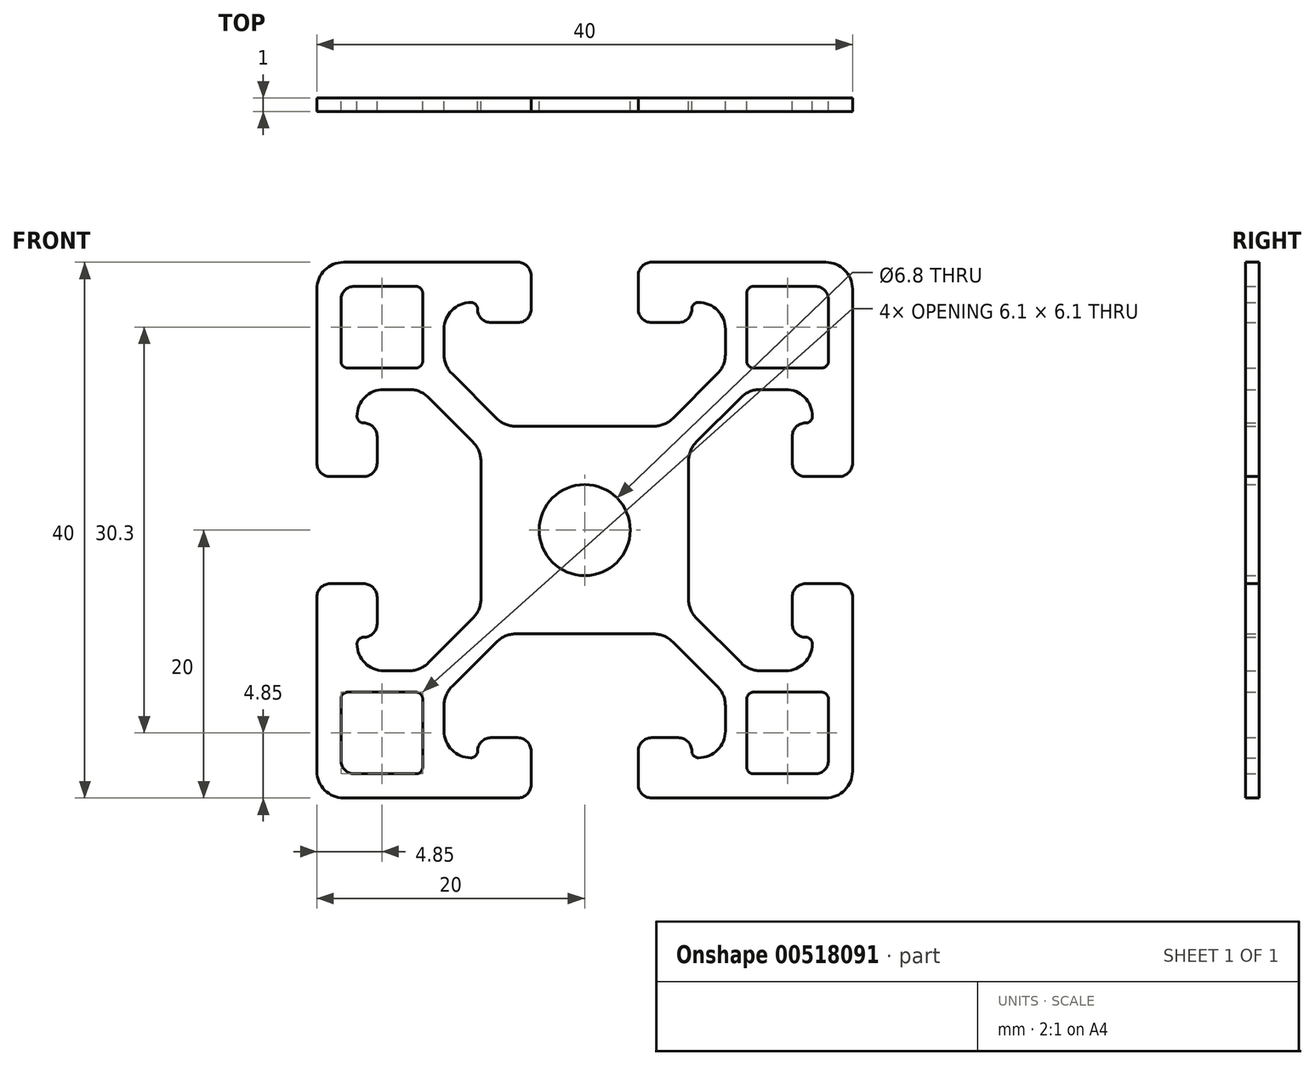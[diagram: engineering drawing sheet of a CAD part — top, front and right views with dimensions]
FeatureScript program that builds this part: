
annotation { "Feature Type Name" : "Feature", "Feature Type Description" : "" }
export const myFeature = defineFeature(function(context is Context, id is Id, definition is map)
    precondition{}
    {
        {
            var Q0;
            Q0=qCreatedBy(makeId("Front.planeOp"),FACE);
            var sketch = newSketch(context, id + "F0", { "sketchPlane" : qUnion([Q0])});
            skLineSegment(sketch, "E0", {"start": v(-20, 18) * mm, "end": v(-20, 5) * mm});
            skLineSegment(sketch, "E1", {"start": v(-19, 4) * mm, "end": v(-16.5, 4) * mm});
            skLineSegment(sketch, "E2", {"start": v(-15.5, 5) * mm, "end": v(-15.5, 7) * mm});
            skLineSegment(sketch, "E3", {"start": v(-16.5, 8) * mm, "end": v(-16.5, 8) * mm});
            skLineSegment(sketch, "E4", {"start": v(-2.4, 2.4) * mm, "end": v(-12.25, 12.25) * mm});
            skArc(sketch, "E5", {"start": v(-17, 8.5) * mm, "mid": v(-16.85, 8.15) * mm, "end": v(-16.5, 8) * mm});
            skArc(sketch, "E6", {"start": v(-15, 10.5) * mm, "mid": v(-16.41, 9.91) * mm, "end": v(-17, 8.5) * mm});
            skLineSegment(sketch, "E7", {"start": v(-15, 10.5) * mm, "end": v(-13.1, 10.5) * mm});
            skArc(sketch, "E8.filletArc", {"start": v(-20, 5) * mm, "mid": v(-19.7, 4.3) * mm, "end": v(-19, 4) * mm});
            skArc(sketch, "E9", {"start": v(-11.68, 9.91) * mm, "mid": v(-12.33, 10.35) * mm, "end": v(-13.1, 10.5) * mm});
            skLineSegment(sketch, "E10", {"start": v(-11.68, 9.91) * mm, "end": v(-8.34, 6.57) * mm});
            skArc(sketch, "E11", {"start": v(-8.34, 6.57) * mm, "mid": v(-7.9, 5.92) * mm, "end": v(-7.75, 5.15) * mm});
            skLineSegment(sketch, "E12", {"start": v(-18.2, 17.2) * mm, "end": v(-18.2, 12.6) * mm});
            skLineSegment(sketch, "E13", {"start": v(-17.7, 12.1) * mm, "end": v(-12.6, 12.1) * mm});
            skArc(sketch, "E14", {"start": v(-19.41, 19.41) * mm, "mid": v(-19.85, 18.77) * mm, "end": v(-20, 18) * mm});
            skArc(sketch, "E15", {"start": v(-17.9, 17.9) * mm, "mid": v(-18.12, 17.58) * mm, "end": v(-18.2, 17.2) * mm});
            skPoint(sketch, "E16.visualSharp", {"position": v(-15.5, 4) * mm});
            skArc(sketch, "E16.filletArc", {"start": v(-16.5, 4) * mm, "mid": v(-15.8, 4.3) * mm, "end": v(-15.5, 5) * mm});
            skPoint(sketch, "E17.visualSharp", {"position": v(-15.5, 8) * mm});
            skArc(sketch, "E17.filletArc", {"start": v(-15.5, 7) * mm, "mid": v(-15.8, 7.7) * mm, "end": v(-16.5, 8) * mm});
            skPoint(sketch, "E18.visualSharp", {"position": v(-18.2, 12.1) * mm});
            skArc(sketch, "E18.filletArc", {"start": v(-18.2, 12.6) * mm, "mid": v(-18.05, 12.25) * mm, "end": v(-17.7, 12.1) * mm});
            skArc(sketch, "E19", {"start": v(-12.6, 12.1) * mm, "mid": v(-12.4, 12.14) * mm, "end": v(-12.25, 12.25) * mm});
            skLineSegment(sketch, "E20.trimOffspring", {"start": v(-17.9, 17.9) * mm, "end": v(-19.41, 19.41) * mm});
            skLineSegment(sketch, "E21", {"start": v(-7.75, 5.15) * mm, "end": v(-7.75, 0) * mm});
            skLineSegment(sketch, "E22", {"start": v(-7.75, 0) * mm, "end": v(-3.4, 0) * mm});
            skArc(sketch, "E23", {"start": v(-2.4, 2.4) * mm, "mid": v(-3.14, 1.3) * mm, "end": v(-3.4, 0) * mm});
            skSolve(sketch);
        }
        {
            var Q0;
            Q0=makeQuery(id+"F0.imprint","IMPRINT",FACE,{"disambiguationData":[TD([[makeQuery(id+"F0.imprint","IMPRINT",EDGE,{"derivedFrom":sQuery(id+"F0.wireOp",EDGE,"E0")}),1.0]])]});
            extrude(context, id + "F1", {"entities" : qUnion([Q0]), "depth" : 1 * mm, "offsetDistance" : 25 * mm});
        }
        {
            var Q0;
            Q0=makeQuery(id+"F1.opExtrude","SWEPT_BODY",BODY,{"disambiguationData":[OSD([sQuery(id+"F0.wireOp",EDGE,"E0"),sQuery(id+"F0.wireOp",EDGE,"E1"),sQuery(id+"F0.wireOp",EDGE,"E2"),sQuery(id+"F0.wireOp",EDGE,"E3"),sQuery(id+"F0.wireOp",EDGE,"E4"),sQuery(id+"F0.wireOp",EDGE,"E5"),sQuery(id+"F0.wireOp",EDGE,"E6"),sQuery(id+"F0.wireOp",EDGE,"E7"),sQuery(id+"F0.wireOp",EDGE,"E8.filletArc"),sQuery(id+"F0.wireOp",EDGE,"E9"),sQuery(id+"F0.wireOp",EDGE,"E10"),sQuery(id+"F0.wireOp",EDGE,"E11"),sQuery(id+"F0.wireOp",EDGE,"E12"),sQuery(id+"F0.wireOp",EDGE,"E13"),sQuery(id+"F0.wireOp",EDGE,"E14"),sQuery(id+"F0.wireOp",EDGE,"E15"),sQuery(id+"F0.wireOp",EDGE,"E16.filletArc"),sQuery(id+"F0.wireOp",EDGE,"E17.filletArc"),sQuery(id+"F0.wireOp",EDGE,"E18.filletArc"),sQuery(id+"F0.wireOp",EDGE,"E19"),sQuery(id+"F0.wireOp",EDGE,"E20.trimOffspring"),sQuery(id+"F0.wireOp",EDGE,"E21"),sQuery(id+"F0.wireOp",EDGE,"E22"),sQuery(id+"F0.wireOp",EDGE,"E23")])]});
            var Q1;
            Q1=makeQuery(id+"F1.opExtrude","SWEPT_FACE",FACE,{"disambiguationData":[OSD([sQuery(id+"F0.wireOp",EDGE,"E4")])]});
            mirror(context, id + "F2", {"operationType" : NewBodyOperationType.ADD, "entities" : qUnion([Q0]), "mirrorPlane" : qUnion([Q1])});
        }
        {
            var Q0;
            Q0=makeQuery(id+"F1.opExtrude","SWEPT_BODY",BODY,{"disambiguationData":[OSD([sQuery(id+"F0.wireOp",EDGE,"E0"),sQuery(id+"F0.wireOp",EDGE,"E1"),sQuery(id+"F0.wireOp",EDGE,"E2"),sQuery(id+"F0.wireOp",EDGE,"E3"),sQuery(id+"F0.wireOp",EDGE,"E4"),sQuery(id+"F0.wireOp",EDGE,"E5"),sQuery(id+"F0.wireOp",EDGE,"E6"),sQuery(id+"F0.wireOp",EDGE,"E7"),sQuery(id+"F0.wireOp",EDGE,"E8.filletArc"),sQuery(id+"F0.wireOp",EDGE,"E9"),sQuery(id+"F0.wireOp",EDGE,"E10"),sQuery(id+"F0.wireOp",EDGE,"E11"),sQuery(id+"F0.wireOp",EDGE,"E12"),sQuery(id+"F0.wireOp",EDGE,"E13"),sQuery(id+"F0.wireOp",EDGE,"E14"),sQuery(id+"F0.wireOp",EDGE,"E15"),sQuery(id+"F0.wireOp",EDGE,"E16.filletArc"),sQuery(id+"F0.wireOp",EDGE,"E17.filletArc"),sQuery(id+"F0.wireOp",EDGE,"E18.filletArc"),sQuery(id+"F0.wireOp",EDGE,"E19"),sQuery(id+"F0.wireOp",EDGE,"E20.trimOffspring"),sQuery(id+"F0.wireOp",EDGE,"E21"),sQuery(id+"F0.wireOp",EDGE,"E22"),sQuery(id+"F0.wireOp",EDGE,"E23")])]});
            var Q1;
            Q1=makeQuery(id+"F1.opExtrude","SWEPT_FACE",FACE,{"disambiguationData":[OSD([sQuery(id+"F0.wireOp",EDGE,"E22")])]});
            mirror(context, id + "F3", {"operationType" : NewBodyOperationType.ADD, "entities" : qUnion([Q0]), "mirrorPlane" : qUnion([Q1])});
        }
        {
            var Q0;
            Q0=makeQuery(id+"F1.opExtrude","SWEPT_BODY",BODY,{"disambiguationData":[OSD([sQuery(id+"F0.wireOp",EDGE,"E0"),sQuery(id+"F0.wireOp",EDGE,"E1"),sQuery(id+"F0.wireOp",EDGE,"E2"),sQuery(id+"F0.wireOp",EDGE,"E3"),sQuery(id+"F0.wireOp",EDGE,"E4"),sQuery(id+"F0.wireOp",EDGE,"E5"),sQuery(id+"F0.wireOp",EDGE,"E6"),sQuery(id+"F0.wireOp",EDGE,"E7"),sQuery(id+"F0.wireOp",EDGE,"E8.filletArc"),sQuery(id+"F0.wireOp",EDGE,"E9"),sQuery(id+"F0.wireOp",EDGE,"E10"),sQuery(id+"F0.wireOp",EDGE,"E11"),sQuery(id+"F0.wireOp",EDGE,"E12"),sQuery(id+"F0.wireOp",EDGE,"E13"),sQuery(id+"F0.wireOp",EDGE,"E14"),sQuery(id+"F0.wireOp",EDGE,"E15"),sQuery(id+"F0.wireOp",EDGE,"E16.filletArc"),sQuery(id+"F0.wireOp",EDGE,"E17.filletArc"),sQuery(id+"F0.wireOp",EDGE,"E18.filletArc"),sQuery(id+"F0.wireOp",EDGE,"E19"),sQuery(id+"F0.wireOp",EDGE,"E20.trimOffspring"),sQuery(id+"F0.wireOp",EDGE,"E21"),sQuery(id+"F0.wireOp",EDGE,"E22"),sQuery(id+"F0.wireOp",EDGE,"E23")])]});
            var Q1;
            Q1=makeQuery(id+"F2.opPattern","COPY",FACE,{"derivedFrom":makeQuery(id+"F1.opExtrude","SWEPT_FACE",FACE,{"disambiguationData":[OSD([sQuery(id+"F0.wireOp",EDGE,"E22")])]}),"instanceName":"1"});
            mirror(context, id + "F4", {"operationType" : NewBodyOperationType.ADD, "entities" : qUnion([Q0]), "mirrorPlane" : qUnion([Q1])});
        }
    });
